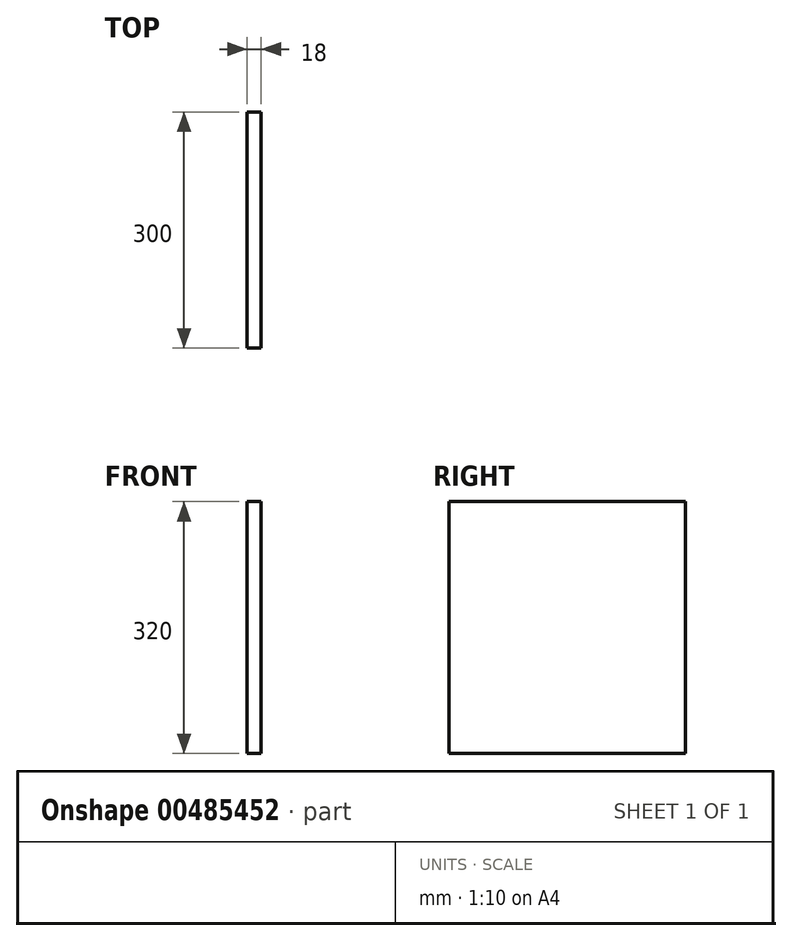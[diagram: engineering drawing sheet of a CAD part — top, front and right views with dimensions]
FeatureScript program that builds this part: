
annotation { "Feature Type Name" : "Feature", "Feature Type Description" : "" }
export const myFeature = defineFeature(function(context is Context, id is Id, definition is map)
    precondition{}
    {
        {
            var Q0;
            Q0=qCreatedBy(makeId("Top.planeOp"),FACE);
            var sketch = newSketch(context, id + "F0", { "sketchPlane" : qUnion([Q0])});
            skLineSegment(sketch, "E0.bottom", {"start": v(9, 150) * mm, "end": v(-9, 150) * mm});
            skLineSegment(sketch, "E0.top", {"start": v(9, -150) * mm, "end": v(-9, -150) * mm});
            skLineSegment(sketch, "E0.left", {"start": v(9, 150) * mm, "end": v(9, -150) * mm});
            skLineSegment(sketch, "E0.right", {"start": v(-9, 150) * mm, "end": v(-9, -150) * mm});
            skPoint(sketch, "E0.middle", {"position": v(0, 0) * mm});
            skSolve(sketch);
        }
        {
            var Q0;
            Q0=makeQuery(id+"F0.imprint","IMPRINT",FACE,{"disambiguationData":[TD([[makeQuery(id+"F0.imprint","IMPRINT",EDGE,{"derivedFrom":sQuery(id+"F0.wireOp",EDGE,"E0.bottom")}),1.0]])]});
            extrude(context, id + "F1", {"entities" : qUnion([Q0]), "depth" : 320 * mm});
        }
    });
